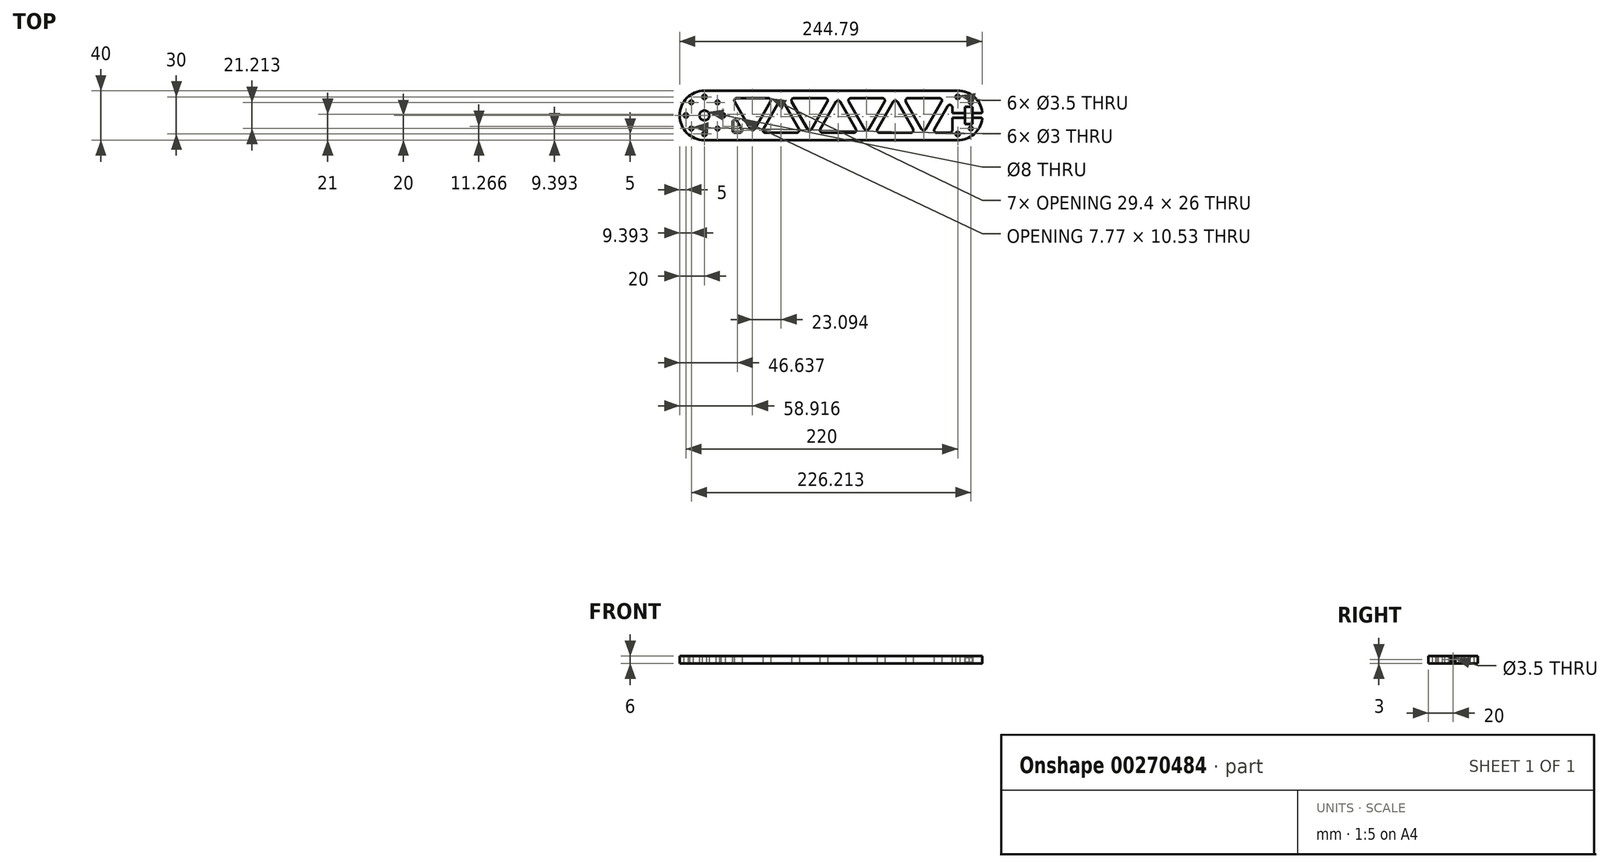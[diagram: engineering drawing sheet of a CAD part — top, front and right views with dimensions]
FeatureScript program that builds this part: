
annotation { "Feature Type Name" : "Feature", "Feature Type Description" : "" }
export const myFeature = defineFeature(function(context is Context, id is Id, definition is map)
    precondition{}
    {
        {
            var Q0;
            Q0=qCreatedBy(makeId("Top.planeOp"),FACE);
            var sketch = newSketch(context, id + "F0", { "sketchPlane" : qUnion([Q0])});
            skLineSegment(sketch, "E0.bottom", {"start": v(0, 0) * mm, "end": v(205, 0) * mm});
            skLineSegment(sketch, "E0.top", {"start": v(0, 40) * mm, "end": v(205, 40) * mm});
            skArc(sketch, "E1", {"start": v(205, 40) * mm, "mid": v(225, 20) * mm, "end": v(205, 0) * mm});
            skArc(sketch, "E2", {"start": v(0, 40) * mm, "mid": v(-20, 20) * mm, "end": v(0, 0) * mm});
            skCircle(sketch, "E3", {"center": v(0, 20) * mm, "radius": 15 * mm, "construction": true});
            skCircle(sketch, "E4", {"center": v(0, 35) * mm, "radius": 1.75 * mm});
            skCircle(sketch, "E5.1.0", {"center": v(-15, 20) * mm, "radius": 1.75 * mm});
            skCircle(sketch, "E5.2.0", {"center": v(0, 5) * mm, "radius": 1.75 * mm});
            skCircle(sketch, "E5.3.0", {"center": v(15, 20) * mm, "radius": 1.75 * mm});
            skLineSegment(sketch, "E6", {"start": v(0, 20) * mm, "end": v(10.6, 30.6) * mm});
            skCircle(sketch, "E7", {"center": v(10.6, 30.6) * mm, "radius": 1.5 * mm});
            skCircle(sketch, "E8.1.0", {"center": v(-10.6, 30.6) * mm, "radius": 1.5 * mm});
            skCircle(sketch, "E8.2.0", {"center": v(-10.6, 9.4) * mm, "radius": 1.5 * mm});
            skCircle(sketch, "E8.3.0", {"center": v(10.6, 9.4) * mm, "radius": 1.5 * mm});
            skCircle(sketch, "E9", {"center": v(0, 20) * mm, "radius": 4 * mm});
            skLineSegment(sketch, "E10", {"start": v(102.5, 40) * mm, "end": v(102.5, 0) * mm, "construction": true});
            skCircle(sketch, "E11.MirrorC", {"center": v(205, 5) * mm, "radius": 1.75 * mm});
            skCircle(sketch, "E12.MirrorC", {"center": v(215.6, 30.6) * mm, "radius": 1.5 * mm});
            skCircle(sketch, "E13.MirrorC", {"center": v(215.6, 9.4) * mm, "radius": 1.5 * mm});
            skLineSegment(sketch, "E14.MirrorCS", {"start": v(205, 20) * mm, "end": v(194.4, 30.6) * mm});
            skCircle(sketch, "E15.MirrorC", {"center": v(205, 20) * mm, "radius": 15 * mm, "construction": true});
            skCircle(sketch, "E16.MirrorC", {"center": v(205, 35) * mm, "radius": 1.75 * mm});
            skSolve(sketch);
        }
        {
            var Q0;
            Q0=qSketchRegion(id+"F0",true);
            extrude(context, id + "F1", {"entities" : qUnion([Q0]), "depth" : 6 * mm});
        }
        {
            var Q0;
            Q0=makeQuery(id+"F1.opExtrude","CAP_FACE",FACE,{"disambiguationData":[OSD([sQuery(id+"F0.wireOp",EDGE,"E0.bottom"),sQuery(id+"F0.wireOp",EDGE,"E0.top"),sQuery(id+"F0.wireOp",EDGE,"E2"),sQuery(id+"F0.wireOp",EDGE,"E4"),sQuery(id+"F0.wireOp",EDGE,"E5.1.0"),sQuery(id+"F0.wireOp",EDGE,"E5.2.0"),sQuery(id+"F0.wireOp",EDGE,"E5.3.0"),sQuery(id+"F0.wireOp",EDGE,"E7"),sQuery(id+"F0.wireOp",EDGE,"E8.1.0"),sQuery(id+"F0.wireOp",EDGE,"E8.2.0"),sQuery(id+"F0.wireOp",EDGE,"E8.3.0"),sQuery(id+"F0.wireOp",EDGE,"E9"),sQuery(id+"F0.wireOp",EDGE,"E11.MirrorC"),sQuery(id+"F0.wireOp",EDGE,"E12.MirrorC"),sQuery(id+"F0.wireOp",EDGE,"E13.MirrorC"),sQuery(id+"F0.wireOp",EDGE,"E1"),sQuery(id+"F0.wireOp",EDGE,"E16.MirrorC")])],"isStart":false});
            var sketch = newSketch(context, id + "F2", { "sketchPlane" : qUnion([Q0])});
            skLineSegment(sketch, "E17.left", {"start": v(22.75, 34) * mm, "end": v(22.75, 6) * mm, "construction": true});
            skLineSegment(sketch, "E17.right", {"start": v(200.57, 26.43) * mm, "end": v(200.57, 6) * mm, "construction": true});
            skLineSegment(sketch, "E18", {"start": v(22.75, 34) * mm, "end": v(55.08, 34) * mm});
            skLineSegment(sketch, "E19", {"start": v(55.08, 34) * mm, "end": v(38.92, 6) * mm});
            skLineSegment(sketch, "E20", {"start": v(38.92, 6) * mm, "end": v(22.75, 34) * mm});
            skLineSegment(sketch, "E21", {"start": v(45.84, 6) * mm, "end": v(62, 34) * mm});
            skLineSegment(sketch, "E22", {"start": v(62, 34) * mm, "end": v(78.18, 6) * mm});
            skLineSegment(sketch, "E23", {"start": v(78.18, 6) * mm, "end": v(45.84, 6) * mm});
            skLineSegment(sketch, "E24", {"start": v(22.75, 6) * mm, "end": v(200.57, 6) * mm, "construction": true});
            skLineSegment(sketch, "E25", {"start": v(55.08, 34) * mm, "end": v(22.75, 34) * mm, "construction": true});
            skPoint(sketch, "E26.visualSharp", {"position": v(22.75, 34) * mm});
            skPoint(sketch, "E27.visualSharp", {"position": v(38.92, 6) * mm});
            skLineSegment(sketch, "E28.1.0.0", {"start": v(101.27, 34) * mm, "end": v(85.1, 6) * mm});
            skPoint(sketch, "E28.1.0.1", {"position": v(68.94, 34) * mm});
            skLineSegment(sketch, "E28.1.0.2", {"start": v(85.1, 6) * mm, "end": v(68.94, 34) * mm});
            skLineSegment(sketch, "E28.1.0.3", {"start": v(108.2, 34) * mm, "end": v(124.36, 6) * mm});
            skLineSegment(sketch, "E28.1.0.4", {"start": v(92.03, 6) * mm, "end": v(108.2, 34) * mm});
            skPoint(sketch, "E28.1.0.5", {"position": v(85.1, 6) * mm});
            skLineSegment(sketch, "E28.1.0.6", {"start": v(101.27, 34) * mm, "end": v(68.94, 34) * mm, "construction": true});
            skLineSegment(sketch, "E28.1.0.7", {"start": v(124.36, 6) * mm, "end": v(92.03, 6) * mm});
            skLineSegment(sketch, "E28.1.0.8", {"start": v(68.94, 34) * mm, "end": v(101.27, 34) * mm});
            skLineSegment(sketch, "E28.2.0.0", {"start": v(147.46, 34) * mm, "end": v(131.3, 6) * mm});
            skPoint(sketch, "E28.2.0.1", {"position": v(115.13, 34) * mm});
            skLineSegment(sketch, "E28.2.0.2", {"start": v(131.3, 6) * mm, "end": v(115.13, 34) * mm});
            skLineSegment(sketch, "E28.2.0.3", {"start": v(154.39, 34) * mm, "end": v(170.55, 6) * mm});
            skLineSegment(sketch, "E28.2.0.4", {"start": v(138.22, 6) * mm, "end": v(154.39, 34) * mm});
            skPoint(sketch, "E28.2.0.5", {"position": v(131.3, 6) * mm});
            skLineSegment(sketch, "E28.2.0.6", {"start": v(147.46, 34) * mm, "end": v(115.13, 34) * mm, "construction": true});
            skLineSegment(sketch, "E28.2.0.7", {"start": v(170.55, 6) * mm, "end": v(138.22, 6) * mm});
            skLineSegment(sketch, "E28.2.0.8", {"start": v(115.13, 34) * mm, "end": v(147.46, 34) * mm});
            skLineSegment(sketch, "E28.direction1", {"start": v(38.92, 6) * mm, "end": v(85.1, 6) * mm, "construction": true});
            skLineSegment(sketch, "E29.0.3.0", {"start": v(193.65, 34) * mm, "end": v(177.48, 6) * mm});
            skPoint(sketch, "E29.3.3.0", {"position": v(161.31, 34) * mm});
            skLineSegment(sketch, "E29.4.3.0", {"start": v(177.48, 6) * mm, "end": v(161.31, 34) * mm});
            skPoint(sketch, "E29.13.3.0", {"position": v(177.48, 6) * mm});
            skLineSegment(sketch, "E29.14.3.0", {"start": v(193.65, 34) * mm, "end": v(161.31, 34) * mm, "construction": true});
            skLineSegment(sketch, "E29.20.3.0", {"start": v(161.31, 34) * mm, "end": v(193.65, 34) * mm});
            skLineSegment(sketch, "E30", {"start": v(200.57, 34) * mm, "end": v(184.4, 6) * mm});
            skLineSegment(sketch, "E31", {"start": v(184.4, 6) * mm, "end": v(200.57, 6) * mm});
            skLineSegment(sketch, "E32", {"start": v(200.57, 6) * mm, "end": v(200.57, 34) * mm});
            skLineSegment(sketch, "E33", {"start": v(22.75, 6) * mm, "end": v(31.99, 6) * mm});
            skLineSegment(sketch, "E34", {"start": v(31.99, 6) * mm, "end": v(22.75, 22) * mm});
            skLineSegment(sketch, "E35", {"start": v(22.75, 22) * mm, "end": v(22.75, 6) * mm});
            skSolve(sketch);
        }
        {
            var Q0;
            Q0=qSketchRegion(id+"F2",true);
            extrude(context, id + "F3", {"entities" : qUnion([Q0]), "operationType" : NewBodyOperationType.REMOVE, "endBound" : BoundingType.THROUGH_ALL, "oppositeDirection" : true, "depth" : 25 * mm});
        }
        {
            var Q0;
            Q0=makeQuery(id+"F3.boolean.opBoolean","COPY",EDGE,{"derivedFrom":makeQuery(id+"F3.opExtrude","SWEPT_EDGE",EDGE,{"disambiguationData":[OSD([sQuery(id+"F2.wireOp",EDGE,"E18"),sQuery(id+"F2.wireOp",EDGE,"E20")])]})});
            var Q1;
            Q1=makeQuery(id+"F3.boolean.opBoolean","COPY",EDGE,{"derivedFrom":makeQuery(id+"F3.opExtrude","SWEPT_EDGE",EDGE,{"disambiguationData":[OSD([sQuery(id+"F2.wireOp",EDGE,"E18"),sQuery(id+"F2.wireOp",EDGE,"E19")])]})});
            var Q2;
            Q2=makeQuery(id+"F3.boolean.opBoolean","COPY",EDGE,{"derivedFrom":makeQuery(id+"F3.opExtrude","SWEPT_EDGE",EDGE,{"disambiguationData":[OSD([sQuery(id+"F2.wireOp",EDGE,"E19"),sQuery(id+"F2.wireOp",EDGE,"E20")])]})});
            var Q3;
            Q3=makeQuery(id+"F3.boolean.opBoolean","COPY",EDGE,{"derivedFrom":makeQuery(id+"F3.opExtrude","SWEPT_EDGE",EDGE,{"disambiguationData":[OSD([sQuery(id+"F2.wireOp",EDGE,"E21"),sQuery(id+"F2.wireOp",EDGE,"E23")])]})});
            var Q4;
            Q4=makeQuery(id+"F3.boolean.opBoolean","COPY",EDGE,{"derivedFrom":makeQuery(id+"F3.opExtrude","SWEPT_EDGE",EDGE,{"disambiguationData":[OSD([sQuery(id+"F2.wireOp",EDGE,"E21"),sQuery(id+"F2.wireOp",EDGE,"E22")])]})});
            var Q5;
            Q5=makeQuery(id+"F3.boolean.opBoolean","COPY",EDGE,{"derivedFrom":makeQuery(id+"F3.opExtrude","SWEPT_EDGE",EDGE,{"disambiguationData":[OSD([sQuery(id+"F2.wireOp",EDGE,"E22"),sQuery(id+"F2.wireOp",EDGE,"E23")])]})});
            var Q6;
            Q6=makeQuery(id+"F3.boolean.opBoolean","COPY",EDGE,{"derivedFrom":makeQuery(id+"F3.opExtrude","SWEPT_EDGE",EDGE,{"disambiguationData":[OSD([sQuery(id+"F2.wireOp",EDGE,"E34"),sQuery(id+"F2.wireOp",EDGE,"E35")])]})});
            var Q7;
            Q7=makeQuery(id+"F3.boolean.opBoolean","COPY",EDGE,{"derivedFrom":makeQuery(id+"F3.opExtrude","SWEPT_EDGE",EDGE,{"disambiguationData":[OSD([sQuery(id+"F2.wireOp",EDGE,"E33"),sQuery(id+"F2.wireOp",EDGE,"E35")])]})});
            var Q8;
            Q8=makeQuery(id+"F3.boolean.opBoolean","COPY",EDGE,{"derivedFrom":makeQuery(id+"F3.opExtrude","SWEPT_EDGE",EDGE,{"disambiguationData":[OSD([sQuery(id+"F2.wireOp",EDGE,"E33"),sQuery(id+"F2.wireOp",EDGE,"E34")])]})});
            var Q9;
            Q9=makeQuery(id+"F3.boolean.opBoolean","COPY",EDGE,{"derivedFrom":makeQuery(id+"F3.opExtrude","SWEPT_EDGE",EDGE,{"disambiguationData":[OSD([sQuery(id+"F2.wireOp",EDGE,"E28.1.0.2"),sQuery(id+"F2.wireOp",EDGE,"E28.1.0.8")])]})});
            var Q10;
            Q10=makeQuery(id+"F3.boolean.opBoolean","COPY",EDGE,{"derivedFrom":makeQuery(id+"F3.opExtrude","SWEPT_EDGE",EDGE,{"disambiguationData":[OSD([sQuery(id+"F2.wireOp",EDGE,"E28.1.0.0"),sQuery(id+"F2.wireOp",EDGE,"E28.1.0.8")])]})});
            var Q11;
            Q11=makeQuery(id+"F3.boolean.opBoolean","COPY",EDGE,{"derivedFrom":makeQuery(id+"F3.opExtrude","SWEPT_EDGE",EDGE,{"disambiguationData":[OSD([sQuery(id+"F2.wireOp",EDGE,"E28.1.0.0"),sQuery(id+"F2.wireOp",EDGE,"E28.1.0.2")])]})});
            var Q12;
            Q12=makeQuery(id+"F3.boolean.opBoolean","COPY",EDGE,{"derivedFrom":makeQuery(id+"F3.opExtrude","SWEPT_EDGE",EDGE,{"disambiguationData":[OSD([sQuery(id+"F2.wireOp",EDGE,"E28.1.0.4"),sQuery(id+"F2.wireOp",EDGE,"E28.1.0.7")])]})});
            var Q13;
            Q13=makeQuery(id+"F3.boolean.opBoolean","COPY",EDGE,{"derivedFrom":makeQuery(id+"F3.opExtrude","SWEPT_EDGE",EDGE,{"disambiguationData":[OSD([sQuery(id+"F2.wireOp",EDGE,"E28.1.0.3"),sQuery(id+"F2.wireOp",EDGE,"E28.1.0.4")])]})});
            var Q14;
            Q14=makeQuery(id+"F3.boolean.opBoolean","COPY",EDGE,{"derivedFrom":makeQuery(id+"F3.opExtrude","SWEPT_EDGE",EDGE,{"disambiguationData":[OSD([sQuery(id+"F2.wireOp",EDGE,"E28.1.0.3"),sQuery(id+"F2.wireOp",EDGE,"E28.1.0.7")])]})});
            var Q15;
            Q15=makeQuery(id+"F3.boolean.opBoolean","COPY",EDGE,{"derivedFrom":makeQuery(id+"F3.opExtrude","SWEPT_EDGE",EDGE,{"disambiguationData":[OSD([sQuery(id+"F2.wireOp",EDGE,"E28.2.0.2"),sQuery(id+"F2.wireOp",EDGE,"E28.2.0.8")])]})});
            var Q16;
            Q16=makeQuery(id+"F3.boolean.opBoolean","COPY",EDGE,{"derivedFrom":makeQuery(id+"F3.opExtrude","SWEPT_EDGE",EDGE,{"disambiguationData":[OSD([sQuery(id+"F2.wireOp",EDGE,"E29.4.3.0"),sQuery(id+"F2.wireOp",EDGE,"E29.20.3.0")])]})});
            var Q17;
            Q17=makeQuery(id+"F3.boolean.opBoolean","COPY",EDGE,{"derivedFrom":makeQuery(id+"F3.opExtrude","SWEPT_EDGE",EDGE,{"disambiguationData":[OSD([sQuery(id+"F2.wireOp",EDGE,"E28.2.0.0"),sQuery(id+"F2.wireOp",EDGE,"E28.2.0.8")])]})});
            var Q18;
            Q18=makeQuery(id+"F3.boolean.opBoolean","COPY",EDGE,{"derivedFrom":makeQuery(id+"F3.opExtrude","SWEPT_EDGE",EDGE,{"disambiguationData":[OSD([sQuery(id+"F2.wireOp",EDGE,"E29.0.3.0"),sQuery(id+"F2.wireOp",EDGE,"E29.20.3.0")])]})});
            var Q19;
            Q19=makeQuery(id+"F3.boolean.opBoolean","COPY",EDGE,{"derivedFrom":makeQuery(id+"F3.opExtrude","SWEPT_EDGE",EDGE,{"disambiguationData":[OSD([sQuery(id+"F2.wireOp",EDGE,"E28.2.0.0"),sQuery(id+"F2.wireOp",EDGE,"E28.2.0.2")])]})});
            var Q20;
            Q20=makeQuery(id+"F3.boolean.opBoolean","COPY",EDGE,{"derivedFrom":makeQuery(id+"F3.opExtrude","SWEPT_EDGE",EDGE,{"disambiguationData":[OSD([sQuery(id+"F2.wireOp",EDGE,"E28.2.0.3"),sQuery(id+"F2.wireOp",EDGE,"E28.2.0.4")])]})});
            var Q21;
            Q21=makeQuery(id+"F3.boolean.opBoolean","COPY",EDGE,{"derivedFrom":makeQuery(id+"F3.opExtrude","SWEPT_EDGE",EDGE,{"disambiguationData":[OSD([sQuery(id+"F2.wireOp",EDGE,"E28.2.0.3"),sQuery(id+"F2.wireOp",EDGE,"E28.2.0.7")])]})});
            var Q22;
            Q22=makeQuery(id+"F3.boolean.opBoolean","COPY",EDGE,{"derivedFrom":makeQuery(id+"F3.opExtrude","SWEPT_EDGE",EDGE,{"disambiguationData":[OSD([sQuery(id+"F2.wireOp",EDGE,"E28.2.0.4"),sQuery(id+"F2.wireOp",EDGE,"E28.2.0.7")])]})});
            var Q23;
            Q23=makeQuery(id+"F3.boolean.opBoolean","COPY",EDGE,{"derivedFrom":makeQuery(id+"F3.opExtrude","SWEPT_EDGE",EDGE,{"disambiguationData":[OSD([sQuery(id+"F2.wireOp",EDGE,"E31"),sQuery(id+"F2.wireOp",EDGE,"E32")])]})});
            var Q24;
            Q24=makeQuery(id+"F3.boolean.opBoolean","COPY",EDGE,{"derivedFrom":makeQuery(id+"F3.opExtrude","SWEPT_EDGE",EDGE,{"disambiguationData":[OSD([sQuery(id+"F2.wireOp",EDGE,"E30"),sQuery(id+"F2.wireOp",EDGE,"E31")])]})});
            var Q25;
            Q25=makeQuery(id+"F3.boolean.opBoolean","COPY",EDGE,{"derivedFrom":makeQuery(id+"F3.opExtrude","SWEPT_EDGE",EDGE,{"disambiguationData":[OSD([sQuery(id+"F2.wireOp",EDGE,"E30"),sQuery(id+"F2.wireOp",EDGE,"E32")])]})});
            var Q26;
            Q26=makeQuery(id+"F3.boolean.opBoolean","COPY",EDGE,{"derivedFrom":makeQuery(id+"F3.opExtrude","SWEPT_EDGE",EDGE,{"disambiguationData":[OSD([sQuery(id+"F2.wireOp",EDGE,"E29.0.3.0"),sQuery(id+"F2.wireOp",EDGE,"E29.4.3.0")])]})});
            fillet(context, id + "F4", {"entities" : qUnion([Q0, Q1, Q2, Q3, Q4, Q5, Q6, Q7, Q8, Q9, Q10, Q11, Q12, Q13, Q14, Q15, Q16, Q17, Q18, Q19, Q20, Q21, Q22, Q23, Q24, Q25, Q26]), "radius" : 2 * mm, "tangentPropagation" : true, "allowEdgeOverflow" : false});
        }
        {
            var Q0;
            Q0=qCreatedBy(makeId("Top.planeOp"),FACE);
            var sketch = newSketch(context, id + "F5", { "sketchPlane" : qUnion([Q0])});
            skLineSegment(sketch, "E36", {"start": v(31.2, 0) * mm, "end": v(31.2, 7) * mm});
            skLineSegment(sketch, "E37", {"start": v(31.2, 7) * mm, "end": v(27.2, 7) * mm});
            skArc(sketch, "E38", {"start": v(27.2, 7) * mm, "mid": v(10.89, 14.04) * mm, "end": v(0, 0) * mm});
            skLineSegment(sketch, "E39", {"start": v(31.2, 0) * mm, "end": v(0, 0) * mm});
            skSolve(sketch);
        }
        {
            var Q0;
            Q0=qSketchRegion(id+"F5",true);
            var Q1;
            Q1=sQuery(id+"F5.wireOp",EDGE,"E39");
            revolve(context, id + "F6", {"entities" : qUnion([Q0]), "axis" : qUnion([Q1]), "revolveType" : RevolveType.FULL});
        }
        {
            var Q0;
            Q0=makeQuery(id+"F1.opExtrude","SWEPT_BODY",BODY,{"disambiguationData":[OSD([sQuery(id+"F0.wireOp",EDGE,"E0.bottom"),sQuery(id+"F0.wireOp",EDGE,"E0.top"),sQuery(id+"F0.wireOp",EDGE,"E2"),sQuery(id+"F0.wireOp",EDGE,"E4"),sQuery(id+"F0.wireOp",EDGE,"E5.1.0"),sQuery(id+"F0.wireOp",EDGE,"E5.2.0"),sQuery(id+"F0.wireOp",EDGE,"E5.3.0"),sQuery(id+"F0.wireOp",EDGE,"E7"),sQuery(id+"F0.wireOp",EDGE,"E8.1.0"),sQuery(id+"F0.wireOp",EDGE,"E8.2.0"),sQuery(id+"F0.wireOp",EDGE,"E8.3.0"),sQuery(id+"F0.wireOp",EDGE,"E9"),sQuery(id+"F0.wireOp",EDGE,"E11.MirrorC"),sQuery(id+"F0.wireOp",EDGE,"E12.MirrorC"),sQuery(id+"F0.wireOp",EDGE,"E13.MirrorC"),sQuery(id+"F0.wireOp",EDGE,"E1"),sQuery(id+"F0.wireOp",EDGE,"E16.MirrorC")])]});
            transform(context, id + "F7", {"entities" : qUnion([Q0]), "transformType" : TransformType.TRANSLATION_3D, "dx" : 0 * mm, "dy" : 0 * mm, "dz" : 6 * mm, "makeCopy" : true});
        }
        {
            var Q0;
            Q0=makeQuery(id+"F7.opPattern","COPY",BODY,{"derivedFrom":makeQuery(id+"F1.opExtrude","SWEPT_BODY",BODY,{"disambiguationData":[OSD([sQuery(id+"F0.wireOp",EDGE,"E0.bottom"),sQuery(id+"F0.wireOp",EDGE,"E0.top"),sQuery(id+"F0.wireOp",EDGE,"E2"),sQuery(id+"F0.wireOp",EDGE,"E4"),sQuery(id+"F0.wireOp",EDGE,"E5.1.0"),sQuery(id+"F0.wireOp",EDGE,"E5.2.0"),sQuery(id+"F0.wireOp",EDGE,"E5.3.0"),sQuery(id+"F0.wireOp",EDGE,"E7"),sQuery(id+"F0.wireOp",EDGE,"E8.1.0"),sQuery(id+"F0.wireOp",EDGE,"E8.2.0"),sQuery(id+"F0.wireOp",EDGE,"E8.3.0"),sQuery(id+"F0.wireOp",EDGE,"E9"),sQuery(id+"F0.wireOp",EDGE,"E11.MirrorC"),sQuery(id+"F0.wireOp",EDGE,"E12.MirrorC"),sQuery(id+"F0.wireOp",EDGE,"E13.MirrorC"),sQuery(id+"F0.wireOp",EDGE,"E1"),sQuery(id+"F0.wireOp",EDGE,"E16.MirrorC")])]}),"instanceName":"1"});
            transform(context, id + "F8", {"entities" : qUnion([Q0]), "transformType" : TransformType.TRANSLATION_3D, "dx" : 0 * mm, "dy" : 0 * mm, "dz" : 6 * mm, "makeCopy" : true});
        }
        {
            var Q0;
            Q0=makeQuery(id+"F6.opRevolve","SWEPT_FACE",FACE,{"disambiguationData":[OSD([sQuery(id+"F5.wireOp",EDGE,"E36")])]});
            var sketch = newSketch(context, id + "F9", { "sketchPlane" : qUnion([Q0])});
            skCircle(sketch, "E40", {"center": v(0, 0) * mm, "radius": 2 * mm});
            skSolve(sketch);
        }
        {
            var Q0;
            Q0=qSketchRegion(id+"F9",true);
            extrude(context, id + "F10", {"entities" : qUnion([Q0]), "operationType" : NewBodyOperationType.REMOVE, "oppositeDirection" : true, "depth" : 20 * mm});
        }
        {
            var Q0;
            Q0=makeQuery(id+"F6.opRevolve","SWEPT_BODY",BODY,{"disambiguationData":[OSD([sQuery(id+"F5.wireOp",EDGE,"E36"),sQuery(id+"F5.wireOp",EDGE,"E37"),sQuery(id+"F5.wireOp",EDGE,"E38"),sQuery(id+"F5.wireOp",EDGE,"E39")])]});
            var Q1;
            Q1=makeQuery(id+"F1.opExtrude","SWEPT_BODY",BODY,{"disambiguationData":[OSD([sQuery(id+"F0.wireOp",EDGE,"E0.bottom"),sQuery(id+"F0.wireOp",EDGE,"E0.top"),sQuery(id+"F0.wireOp",EDGE,"E2"),sQuery(id+"F0.wireOp",EDGE,"E4"),sQuery(id+"F0.wireOp",EDGE,"E5.1.0"),sQuery(id+"F0.wireOp",EDGE,"E5.2.0"),sQuery(id+"F0.wireOp",EDGE,"E5.3.0"),sQuery(id+"F0.wireOp",EDGE,"E7"),sQuery(id+"F0.wireOp",EDGE,"E8.1.0"),sQuery(id+"F0.wireOp",EDGE,"E8.2.0"),sQuery(id+"F0.wireOp",EDGE,"E8.3.0"),sQuery(id+"F0.wireOp",EDGE,"E9"),sQuery(id+"F0.wireOp",EDGE,"E11.MirrorC"),sQuery(id+"F0.wireOp",EDGE,"E12.MirrorC"),sQuery(id+"F0.wireOp",EDGE,"E13.MirrorC"),sQuery(id+"F0.wireOp",EDGE,"E1"),sQuery(id+"F0.wireOp",EDGE,"E16.MirrorC")])]});
            var Q2;
            Q2=makeQuery(id+"F8.opPattern","COPY",BODY,{"derivedFrom":makeQuery(id+"F7.opPattern","COPY",BODY,{"derivedFrom":makeQuery(id+"F1.opExtrude","SWEPT_BODY",BODY,{"disambiguationData":[OSD([sQuery(id+"F0.wireOp",EDGE,"E0.bottom"),sQuery(id+"F0.wireOp",EDGE,"E0.top"),sQuery(id+"F0.wireOp",EDGE,"E2"),sQuery(id+"F0.wireOp",EDGE,"E4"),sQuery(id+"F0.wireOp",EDGE,"E5.1.0"),sQuery(id+"F0.wireOp",EDGE,"E5.2.0"),sQuery(id+"F0.wireOp",EDGE,"E5.3.0"),sQuery(id+"F0.wireOp",EDGE,"E7"),sQuery(id+"F0.wireOp",EDGE,"E8.1.0"),sQuery(id+"F0.wireOp",EDGE,"E8.2.0"),sQuery(id+"F0.wireOp",EDGE,"E8.3.0"),sQuery(id+"F0.wireOp",EDGE,"E9"),sQuery(id+"F0.wireOp",EDGE,"E11.MirrorC"),sQuery(id+"F0.wireOp",EDGE,"E12.MirrorC"),sQuery(id+"F0.wireOp",EDGE,"E13.MirrorC"),sQuery(id+"F0.wireOp",EDGE,"E1"),sQuery(id+"F0.wireOp",EDGE,"E16.MirrorC")])]}),"instanceName":"1"}),"instanceName":"1"});
            deleteBodies(context, id + "F11", {"entities" : qUnion([Q0, Q1, Q2])});
        }
        {
            var Q0;
            Q0=makeQuery(id+"F7.opPattern","COPY",FACE,{"derivedFrom":makeQuery(id+"F1.opExtrude","CAP_FACE",FACE,{"disambiguationData":[OSD([sQuery(id+"F0.wireOp",EDGE,"E0.bottom"),sQuery(id+"F0.wireOp",EDGE,"E0.top"),sQuery(id+"F0.wireOp",EDGE,"E2"),sQuery(id+"F0.wireOp",EDGE,"E4"),sQuery(id+"F0.wireOp",EDGE,"E5.1.0"),sQuery(id+"F0.wireOp",EDGE,"E5.2.0"),sQuery(id+"F0.wireOp",EDGE,"E5.3.0"),sQuery(id+"F0.wireOp",EDGE,"E7"),sQuery(id+"F0.wireOp",EDGE,"E8.1.0"),sQuery(id+"F0.wireOp",EDGE,"E8.2.0"),sQuery(id+"F0.wireOp",EDGE,"E8.3.0"),sQuery(id+"F0.wireOp",EDGE,"E9"),sQuery(id+"F0.wireOp",EDGE,"E11.MirrorC"),sQuery(id+"F0.wireOp",EDGE,"E12.MirrorC"),sQuery(id+"F0.wireOp",EDGE,"E13.MirrorC"),sQuery(id+"F0.wireOp",EDGE,"E1"),sQuery(id+"F0.wireOp",EDGE,"E16.MirrorC")])],"isStart":false}),"instanceName":"1"});
            var sketch = newSketch(context, id + "F12", { "sketchPlane" : qUnion([Q0])});
            skLineSegment(sketch, "E41.bottom", {"start": v(255, 18.15) * mm, "end": v(217, 18.15) * mm});
            skLineSegment(sketch, "E41.top", {"start": v(255, 21.85) * mm, "end": v(217, 21.85) * mm});
            skLineSegment(sketch, "E41.left", {"start": v(255, 18.15) * mm, "end": v(255, 21.85) * mm});
            skLineSegment(sketch, "E41.right", {"start": v(195, 18.15) * mm, "end": v(195, 21.85) * mm});
            skPoint(sketch, "E41.middle", {"position": v(225, 20) * mm});
            skLineSegment(sketch, "E42", {"start": v(210.9, 21.85) * mm, "end": v(210.9, 26.85) * mm});
            skLineSegment(sketch, "E43", {"start": v(217, 26.85) * mm, "end": v(217, 21.85) * mm});
            skLineSegment(sketch, "E44", {"start": v(217, 18.15) * mm, "end": v(217, 13.15) * mm});
            skLineSegment(sketch, "E45", {"start": v(210.9, 13.15) * mm, "end": v(210.9, 18.15) * mm});
            skLineSegment(sketch, "E46", {"start": v(217, 26.85) * mm, "end": v(210.9, 26.85) * mm});
            skLineSegment(sketch, "E47", {"start": v(210.9, 13.15) * mm, "end": v(217, 13.15) * mm});
            skLineSegment(sketch, "E48.trimOffspring", {"start": v(210.9, 18.15) * mm, "end": v(195, 18.15) * mm});
            skLineSegment(sketch, "E49.trimOffspring", {"start": v(210.9, 21.85) * mm, "end": v(195, 21.85) * mm});
            skPoint(sketch, "E50.trimOffspring.end.orphan", {"position": v(210.9, 21.85) * mm});
            skSolve(sketch);
        }
        {
            var Q0;
            Q0 = qSketchRegion(id + "F12", true);
            extrude(context, id + "F13", {"entities" : qUnion([Q0]), "operationType" : NewBodyOperationType.REMOVE, "endBound" : BoundingType.THROUGH_ALL, "oppositeDirection" : true, "depth" : 25 * mm});
        }
        {
            var Q0;
            Q0=makeQuery(id+"F13.boolean.opBoolean","INTERSECT",EDGE,{"derivedFrom":[makeQuery(id+"F7.opPattern","COPY",FACE,{"derivedFrom":makeQuery(id+"F1.opExtrude","SWEPT_FACE",FACE,{"disambiguationData":[OSD([sQuery(id+"F0.wireOp",EDGE,"E1")])]}),"instanceName":"1"}),makeQuery(id+"F13.opExtrude","SWEPT_FACE",FACE,{"disambiguationData":[OSD([sQuery(id+"F12.wireOp",EDGE,"E41.top")])]})]});
            var Q1;
            Q1=makeQuery(id+"F13.boolean.opBoolean","INTERSECT",EDGE,{"derivedFrom":[makeQuery(id+"F7.opPattern","COPY",FACE,{"derivedFrom":makeQuery(id+"F1.opExtrude","SWEPT_FACE",FACE,{"disambiguationData":[OSD([sQuery(id+"F0.wireOp",EDGE,"E1")])]}),"instanceName":"1"}),makeQuery(id+"F13.opExtrude","SWEPT_FACE",FACE,{"disambiguationData":[OSD([sQuery(id+"F12.wireOp",EDGE,"E41.bottom")])]})]});
            fillet(context, id + "F14", {"entities" : qUnion([Q0, Q1]), "radius" : 1 * mm, "tangentPropagation" : true, "allowEdgeOverflow" : false});
        }
        {
            var Q0;
            Q0=makeQuery(id+"F13.boolean.opBoolean","COPY",FACE,{"derivedFrom":makeQuery(id+"F13.opExtrude","SWEPT_FACE",FACE,{"disambiguationData":[OSD([sQuery(id+"F12.wireOp",EDGE,"E43")])]})});
            var sketch = newSketch(context, id + "F15", { "sketchPlane" : qUnion([Q0])});
            skLineSegment(sketch, "E51.bottom", {"start": v(-26.85, 6) * mm, "end": v(-13.15, 6) * mm});
            skLineSegment(sketch, "E51.top", {"start": v(-26.85, 12) * mm, "end": v(-13.15, 12) * mm});
            skLineSegment(sketch, "E51.left", {"start": v(-26.85, 6) * mm, "end": v(-26.85, 12) * mm});
            skLineSegment(sketch, "E51.right", {"start": v(-13.15, 6) * mm, "end": v(-13.15, 12) * mm});
            skCircle(sketch, "E52", {"center": v(-20, 9) * mm, "radius": 1.75 * mm});
            skPoint(sketch, "E52.centerSnap0", {"position": v(-20, 6) * mm});
            skSolve(sketch);
        }
        {
            var Q0;
            {var subQ2=sQuery(id+"F15.wireOp",EDGE,"E51.left");Q0=makeQuery(id+"F15.imprint","IMPRINT",FACE,{"disambiguationData":[TD([[makeQuery(id+"F15.imprint","IMPRINT",EDGE,{"derivedFrom":subQ2}),-1.0]])]});}
            var Q1;
            {var subQ2=sQuery(id+"F15.wireOp",EDGE,"E51.right");Q1=makeQuery(id+"F15.imprint","IMPRINT",FACE,{"disambiguationData":[TD([[makeQuery(id+"F15.imprint","IMPRINT",EDGE,{"derivedFrom":subQ2}),1.0]])]});}
            extrude(context, id + "F16", {"entities" : qUnion([Q0, Q1]), "depth" : 6 * mm});
        }
    });
